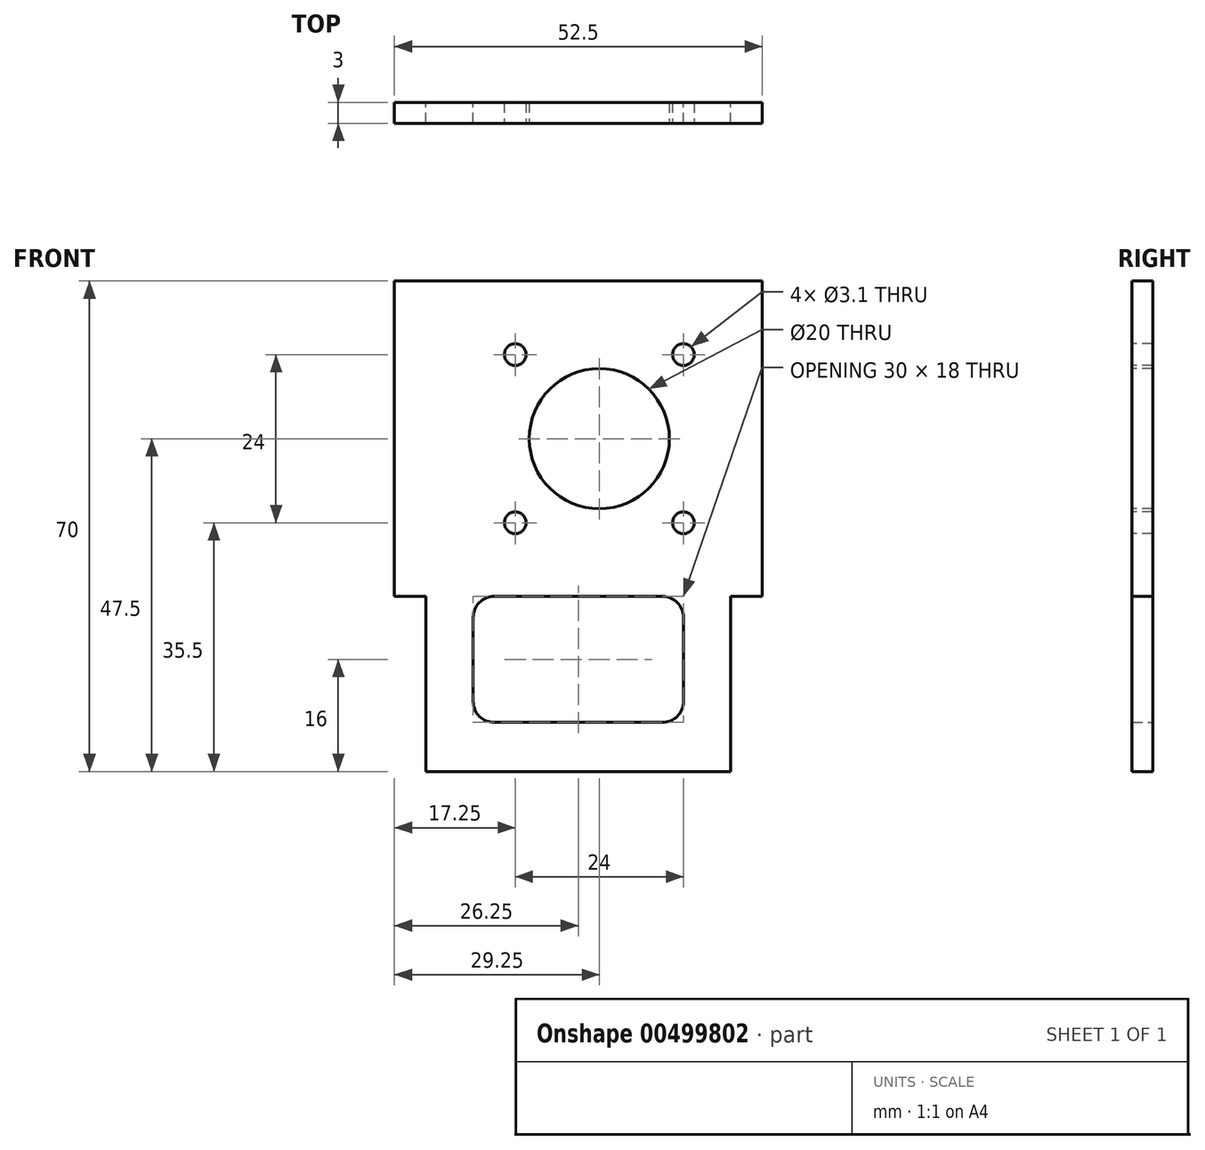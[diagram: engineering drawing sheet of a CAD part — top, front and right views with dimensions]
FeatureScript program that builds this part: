
annotation { "Feature Type Name" : "Feature", "Feature Type Description" : "" }
export const myFeature = defineFeature(function(context is Context, id is Id, definition is map)
    precondition{}
    {
        {
            var Q0;
            Q0=qCreatedBy(makeId("Front.planeOp"),FACE);
            var sketch = newSketch(context, id + "F0", { "sketchPlane" : qUnion([Q0])});
            skLineSegment(sketch, "E0.bottom", {"start": v(26.25, 35) * mm, "end": v(-26.25, 35) * mm, "construction": true});
            skLineSegment(sketch, "E0.top", {"start": v(26.25, -35) * mm, "end": v(-26.25, -35) * mm, "construction": true});
            skLineSegment(sketch, "E0.left", {"start": v(26.25, 35) * mm, "end": v(26.25, -35) * mm, "construction": true});
            skLineSegment(sketch, "E0.right", {"start": v(-26.25, 35) * mm, "end": v(-26.25, -35) * mm, "construction": true});
            skPoint(sketch, "E0.middle", {"position": v(0, 0) * mm});
            skLineSegment(sketch, "E1.bottom", {"start": v(-26.25, -35) * mm, "end": v(26.25, -35) * mm, "construction": true});
            skLineSegment(sketch, "E1.top", {"start": v(-26.25, -10) * mm, "end": v(26.25, -10) * mm, "construction": true});
            skLineSegment(sketch, "E1.left", {"start": v(-26.25, -35) * mm, "end": v(-26.25, -10) * mm, "construction": true});
            skLineSegment(sketch, "E1.right", {"start": v(26.25, -35) * mm, "end": v(26.25, -10) * mm, "construction": true});
            skLineSegment(sketch, "E2.bottom", {"start": v(-26.25, -10) * mm, "end": v(-21.75, -10) * mm, "construction": true});
            skLineSegment(sketch, "E2.top", {"start": v(-26.25, -35) * mm, "end": v(-21.75, -35) * mm, "construction": true});
            skLineSegment(sketch, "E2.left", {"start": v(-26.25, -10) * mm, "end": v(-26.25, -35) * mm, "construction": true});
            skLineSegment(sketch, "E2.right", {"start": v(-21.75, -10) * mm, "end": v(-21.75, -35) * mm, "construction": true});
            skLineSegment(sketch, "E3.bottom", {"start": v(26.25, -10) * mm, "end": v(21.75, -10) * mm, "construction": true});
            skLineSegment(sketch, "E3.top", {"start": v(26.25, -35) * mm, "end": v(21.75, -35) * mm, "construction": true});
            skLineSegment(sketch, "E3.left", {"start": v(26.25, -10) * mm, "end": v(26.25, -35) * mm, "construction": true});
            skLineSegment(sketch, "E3.right", {"start": v(21.75, -10) * mm, "end": v(21.75, -35) * mm, "construction": true});
            skLineSegment(sketch, "E4.bottom", {"start": v(15, -28) * mm, "end": v(-15, -28) * mm, "construction": true});
            skLineSegment(sketch, "E4.top", {"start": v(15, -10) * mm, "end": v(-15, -10) * mm, "construction": true});
            skLineSegment(sketch, "E4.left", {"start": v(15, -28) * mm, "end": v(15, -10) * mm, "construction": true});
            skLineSegment(sketch, "E4.right", {"start": v(-15, -28) * mm, "end": v(-15, -10) * mm, "construction": true});
            skPoint(sketch, "E4.middle", {"position": v(0, -19) * mm});
            skLineSegment(sketch, "E5", {"start": v(-21.75, -35) * mm, "end": v(21.75, -35) * mm});
            skLineSegment(sketch, "E6", {"start": v(21.75, -10) * mm, "end": v(21.75, -35) * mm});
            skLineSegment(sketch, "E7", {"start": v(21.75, -10) * mm, "end": v(26.25, -10) * mm});
            skLineSegment(sketch, "E8", {"start": v(26.25, -10) * mm, "end": v(26.25, 35) * mm});
            skLineSegment(sketch, "E9", {"start": v(26.25, 35) * mm, "end": v(-26.25, 35) * mm});
            skLineSegment(sketch, "E10", {"start": v(-26.25, 35) * mm, "end": v(-26.25, -10) * mm});
            skLineSegment(sketch, "E11", {"start": v(-26.25, -10) * mm, "end": v(-21.75, -10) * mm});
            skLineSegment(sketch, "E12", {"start": v(-21.75, -10) * mm, "end": v(-21.75, -35) * mm});
            skLineSegment(sketch, "E13", {"start": v(-15, -10) * mm, "end": v(15, -10) * mm});
            skLineSegment(sketch, "E14", {"start": v(15, -28) * mm, "end": v(15, -10) * mm});
            skLineSegment(sketch, "E15", {"start": v(-15, -10) * mm, "end": v(-15, -28) * mm});
            skLineSegment(sketch, "E16", {"start": v(15, -28) * mm, "end": v(-15, -28) * mm});
            skSolve(sketch);
        }
        {
            var Q0;
            Q0=makeQuery(id+"F0.imprint","IMPRINT",FACE,{"disambiguationData":[TD([[makeQuery(id+"F0.imprint","IMPRINT",EDGE,{"derivedFrom":sQuery(id+"F0.wireOp",EDGE,"E5")}),1.0]])]});
            extrude(context, id + "F1", {"entities" : qUnion([Q0]), "depth" : 3 * mm, "offsetDistance" : 25 * mm});
        }
        {
            var Q0;
            Q0=makeQuery(id+"F1.opExtrude","SWEPT_EDGE",EDGE,{"disambiguationData":[OSD([sQuery(id+"F0.wireOp",EDGE,"E15"),sQuery(id+"F0.wireOp",EDGE,"E16")])]});
            var Q1;
            Q1=makeQuery(id+"F1.opExtrude","SWEPT_EDGE",EDGE,{"disambiguationData":[OSD([sQuery(id+"F0.wireOp",EDGE,"E14"),sQuery(id+"F0.wireOp",EDGE,"E16")])]});
            var Q2;
            Q2=makeQuery(id+"F1.opExtrude","SWEPT_EDGE",EDGE,{"disambiguationData":[OSD([sQuery(id+"F0.wireOp",EDGE,"E13"),sQuery(id+"F0.wireOp",EDGE,"E14")])]});
            var Q3;
            Q3=makeQuery(id+"F1.opExtrude","SWEPT_EDGE",EDGE,{"disambiguationData":[OSD([sQuery(id+"F0.wireOp",EDGE,"E13"),sQuery(id+"F0.wireOp",EDGE,"E15")])]});
            fillet(context, id + "F2", {"entities" : qUnion([Q0, Q1, Q2, Q3]), "radius" : 3 * mm, "tangentPropagation" : true, "allowEdgeOverflow" : false});
        }
        {
            var Q0;
            Q0=makeQuery(id+"F1.opExtrude","CAP_FACE",FACE,{"disambiguationData":[OSD([sQuery(id+"F0.wireOp",EDGE,"E5"),sQuery(id+"F0.wireOp",EDGE,"E6"),sQuery(id+"F0.wireOp",EDGE,"E7"),sQuery(id+"F0.wireOp",EDGE,"E8"),sQuery(id+"F0.wireOp",EDGE,"E9"),sQuery(id+"F0.wireOp",EDGE,"E10"),sQuery(id+"F0.wireOp",EDGE,"E11"),sQuery(id+"F0.wireOp",EDGE,"E12"),sQuery(id+"F0.wireOp",EDGE,"E13"),sQuery(id+"F0.wireOp",EDGE,"E14"),sQuery(id+"F0.wireOp",EDGE,"E15"),sQuery(id+"F0.wireOp",EDGE,"E16")])],"isStart":false});
            var sketch = newSketch(context, id + "F3", { "sketchPlane" : qUnion([Q0])});
            skLineSegment(sketch, "E17", {"start": v(-26.25, 35) * mm, "end": v(26.25, -10) * mm, "construction": true});
            skLineSegment(sketch, "E18", {"start": v(26.25, -10) * mm, "end": v(-26.25, -10) * mm, "construction": true});
            skLineSegment(sketch, "E19", {"start": v(-26.25, -10) * mm, "end": v(26.25, 35) * mm, "construction": true});
            skPoint(sketch, "E20", {"position": v(0, 12.5) * mm});
            skLineSegment(sketch, "E21", {"start": v(0, 12.5) * mm, "end": v(3, 12.5) * mm, "construction": true});
            skCircle(sketch, "E22", {"center": v(3, 12.5) * mm, "radius": 10 * mm});
            skLineSegment(sketch, "E23.bottom", {"start": v(15, 0.5) * mm, "end": v(-9, 0.5) * mm, "construction": true});
            skLineSegment(sketch, "E23.top", {"start": v(15, 24.5) * mm, "end": v(-9, 24.5) * mm, "construction": true});
            skLineSegment(sketch, "E23.left", {"start": v(15, 0.5) * mm, "end": v(15, 24.5) * mm, "construction": true});
            skLineSegment(sketch, "E23.right", {"start": v(-9, 0.5) * mm, "end": v(-9, 24.5) * mm, "construction": true});
            skCircle(sketch, "E24", {"center": v(-9, 24.5) * mm, "radius": 1.55 * mm});
            skCircle(sketch, "E25", {"center": v(15, 24.5) * mm, "radius": 1.55 * mm});
            skCircle(sketch, "E26", {"center": v(15, 0.5) * mm, "radius": 1.55 * mm});
            skCircle(sketch, "E27", {"center": v(-9, 0.5) * mm, "radius": 1.55 * mm});
            skSolve(sketch);
        }
        {
            var Q0;
            Q0=makeQuery(id+"F3.imprint","IMPRINT",FACE,{"disambiguationData":[TD([[makeQuery(id+"F3.imprint","IMPRINT",EDGE,{"derivedFrom":sQuery(id+"F3.wireOp",EDGE,"E24")}),1.0]])]});
            var Q1;
            Q1=makeQuery(id+"F3.imprint","IMPRINT",FACE,{"disambiguationData":[TD([[makeQuery(id+"F3.imprint","IMPRINT",EDGE,{"derivedFrom":sQuery(id+"F3.wireOp",EDGE,"E25")}),1.0]])]});
            var Q2;
            Q2=makeQuery(id+"F3.imprint","IMPRINT",FACE,{"disambiguationData":[TD([[makeQuery(id+"F3.imprint","IMPRINT",EDGE,{"derivedFrom":sQuery(id+"F3.wireOp",EDGE,"E27")}),1.0]])]});
            var Q3;
            Q3=makeQuery(id+"F3.imprint","IMPRINT",FACE,{"disambiguationData":[TD([[makeQuery(id+"F3.imprint","IMPRINT",EDGE,{"derivedFrom":sQuery(id+"F3.wireOp",EDGE,"E26")}),1.0]])]});
            var Q4;
            Q4=makeQuery(id+"F3.imprint","IMPRINT",FACE,{"disambiguationData":[TD([[makeQuery(id+"F3.imprint","IMPRINT",EDGE,{"derivedFrom":sQuery(id+"F3.wireOp",EDGE,"E22")}),1.0]])]});
            extrude(context, id + "F4", {"entities" : qUnion([Q0, Q1, Q2, Q3, Q4]), "operationType" : NewBodyOperationType.REMOVE, "endBound" : BoundingType.THROUGH_ALL, "oppositeDirection" : true, "depth" : 25 * mm, "offsetDistance" : 25 * mm});
        }
    });
